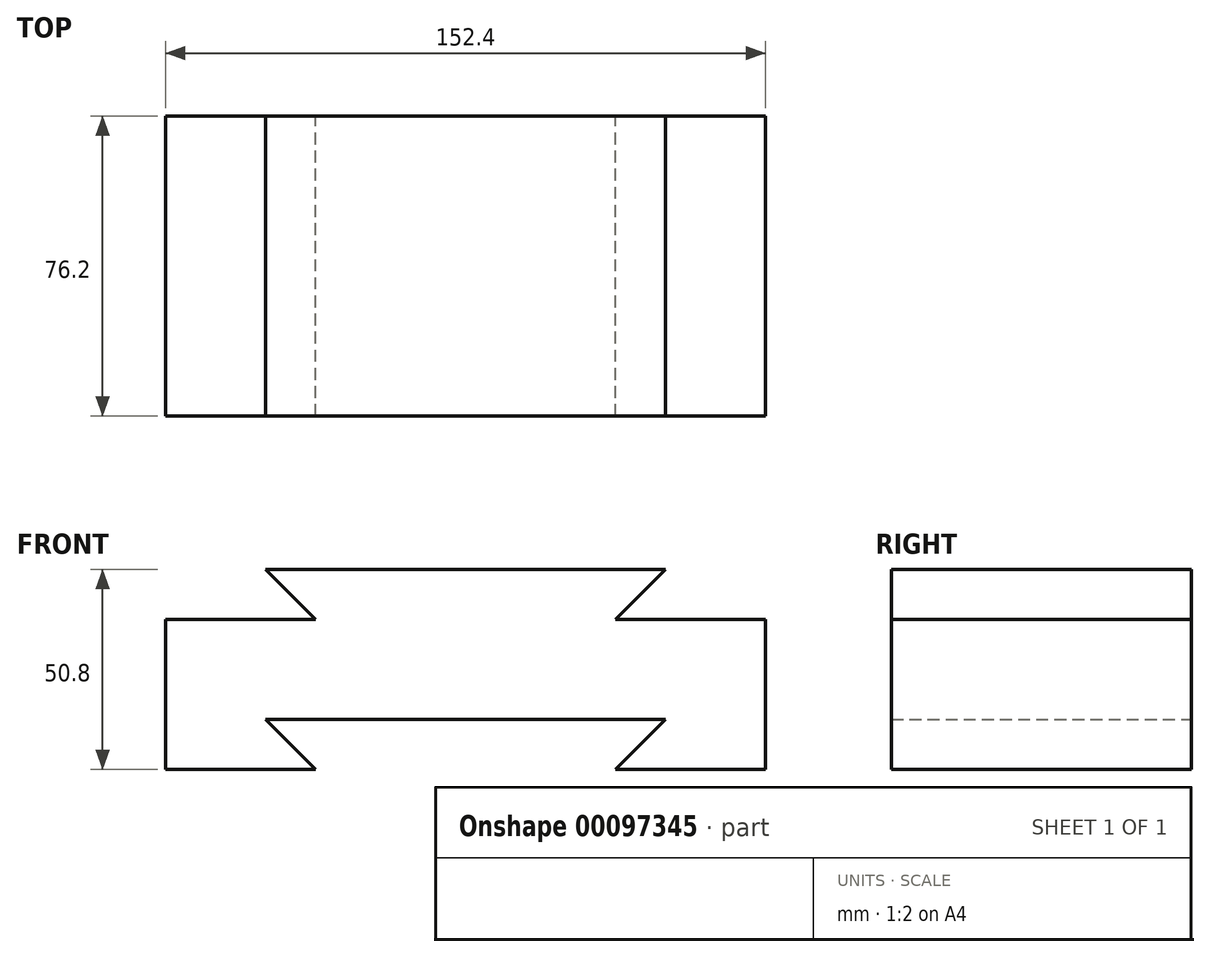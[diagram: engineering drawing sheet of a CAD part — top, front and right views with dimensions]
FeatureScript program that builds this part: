
annotation { "Feature Type Name" : "Feature", "Feature Type Description" : "" }
export const myFeature = defineFeature(function(context is Context, id is Id, definition is map)
    precondition{}
    {
        {
            var Q0;
            Q0=qCreatedBy(makeId("Front.planeOp"),FACE);
            var sketch = newSketch(context, id + "F0", { "sketchPlane" : qUnion([Q0])});
            skLineSegment(sketch, "E0", {"start": v(0, 12.7) * mm, "end": v(50.8, 12.7) * mm});
            skLineSegment(sketch, "E1", {"start": v(50.8, 12.7) * mm, "end": v(38.1, 0) * mm});
            skLineSegment(sketch, "E2", {"start": v(38.1, 0) * mm, "end": v(76.2, 0) * mm});
            skLineSegment(sketch, "E3", {"start": v(76.2, 0) * mm, "end": v(76.2, 38.1) * mm});
            skLineSegment(sketch, "E4", {"start": v(76.2, 38.1) * mm, "end": v(38.1, 38.1) * mm});
            skLineSegment(sketch, "E5", {"start": v(38.1, 38.1) * mm, "end": v(50.8, 50.8) * mm});
            skLineSegment(sketch, "E6", {"start": v(50.8, 50.8) * mm, "end": v(0, 50.8) * mm});
            skLineSegment(sketch, "E7", {"start": v(0, 50.8) * mm, "end": v(0, 12.7) * mm});
            skSolve(sketch);
        }
        {
            var Q0;
            Q0=makeQuery(id+"F0.imprint","IMPRINT",FACE,{"disambiguationData":[TD([[makeQuery(id+"F0.imprint","IMPRINT",EDGE,{"derivedFrom":sQuery(id+"F0.wireOp",EDGE,"E0")}),1.0]])]});
            extrude(context, id + "F1", {"entities" : qUnion([Q0]), "depth" : 76.2 * mm, "symmetric" : true});
        }
        {
            var Q0;
            Q0=makeQuery(id+"F1.opExtrude","SWEPT_BODY",BODY,{"disambiguationData":[OSD([sQuery(id+"F0.wireOp",EDGE,"E0"),sQuery(id+"F0.wireOp",EDGE,"E1"),sQuery(id+"F0.wireOp",EDGE,"E2"),sQuery(id+"F0.wireOp",EDGE,"E3"),sQuery(id+"F0.wireOp",EDGE,"E4"),sQuery(id+"F0.wireOp",EDGE,"E5"),sQuery(id+"F0.wireOp",EDGE,"E6"),sQuery(id+"F0.wireOp",EDGE,"E7")])]});
            var Q1;
            Q1=makeQuery(id+"F1.opExtrude","SWEPT_FACE",FACE,{"disambiguationData":[OSD([sQuery(id+"F0.wireOp",EDGE,"E7")])]});
            mirror(context, id + "F2", {"operationType" : NewBodyOperationType.ADD, "entities" : qUnion([Q0]), "mirrorPlane" : qUnion([Q1])});
        }
    });
